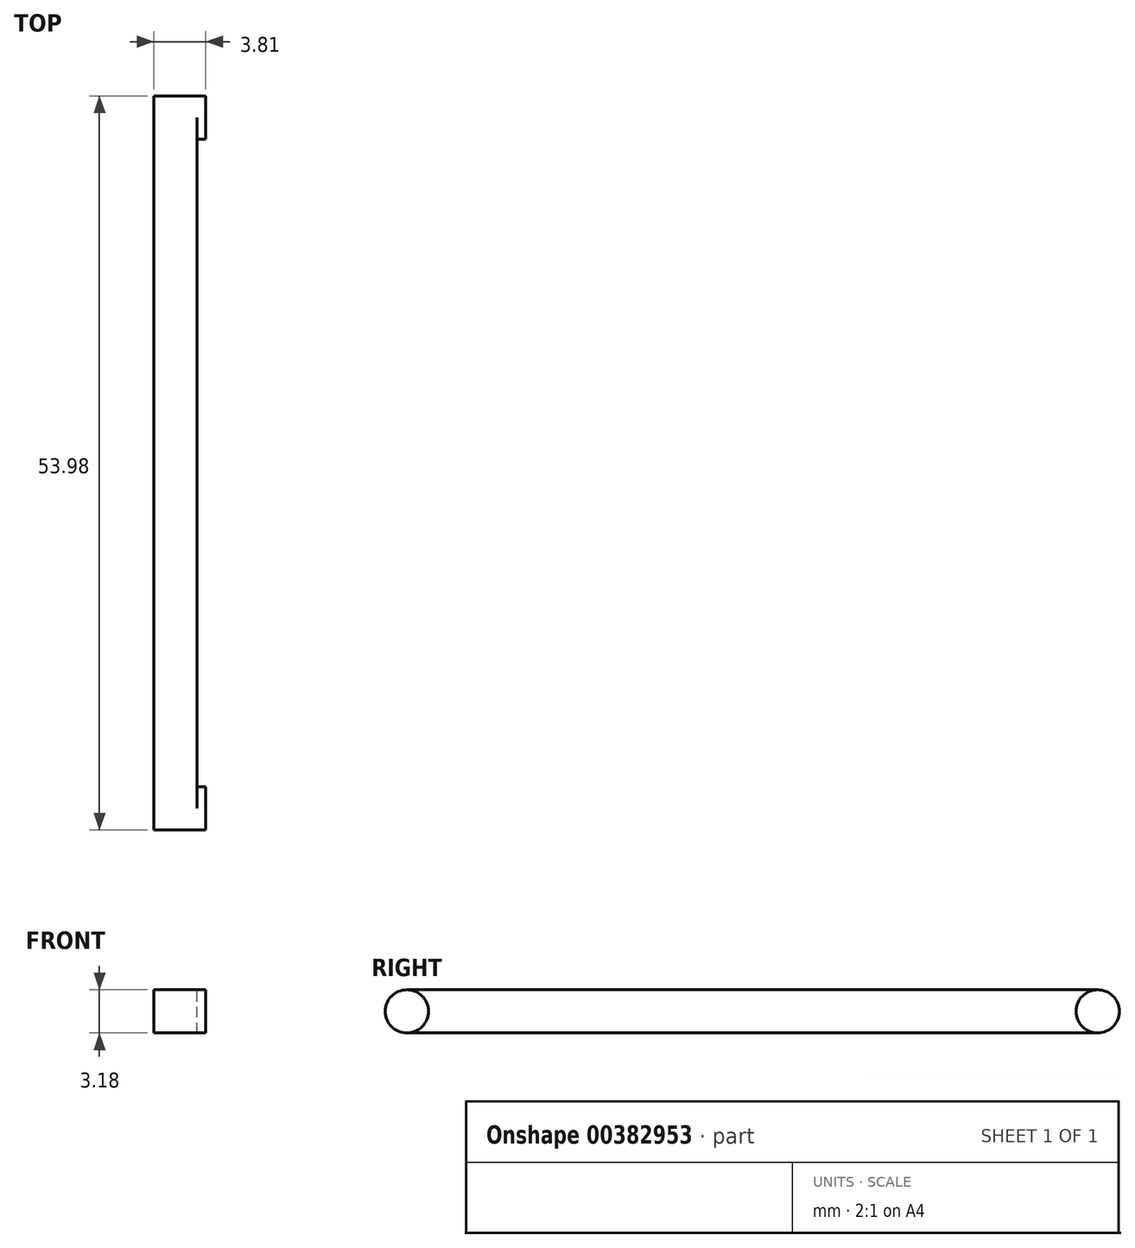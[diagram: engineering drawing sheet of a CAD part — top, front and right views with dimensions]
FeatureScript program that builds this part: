
annotation { "Feature Type Name" : "Feature", "Feature Type Description" : "" }
export const myFeature = defineFeature(function(context is Context, id is Id, definition is map)
    precondition{}
    {
        {
            var Q0;
            Q0=qCreatedBy(makeId("Right.planeOp"),FACE);
            var sketch = newSketch(context, id + "F0", { "sketchPlane" : qUnion([Q0])});
            skLineSegment(sketch, "E0.bottom", {"start": v(25.4, 1.59) * mm, "end": v(-25.4, 1.59) * mm});
            skLineSegment(sketch, "E0.top", {"start": v(25.4, -1.59) * mm, "end": v(-25.4, -1.59) * mm});
            skLineSegment(sketch, "E0.left", {"start": v(25.4, 1.59) * mm, "end": v(25.4, -1.59) * mm});
            skLineSegment(sketch, "E0.right", {"start": v(-25.4, 1.59) * mm, "end": v(-25.4, -1.59) * mm});
            skPoint(sketch, "E0.middle", {"position": v(0, 0) * mm});
            skCircle(sketch, "E1", {"center": v(-25.4, 0) * mm, "radius": 1.59 * mm});
            skCircle(sketch, "E2", {"center": v(25.4, 0) * mm, "radius": 1.59 * mm});
            skSolve(sketch);
        }
        {
            var Q0;
            {var subQ0=sQuery(id+"F0.wireOp",EDGE,"E0.bottom");Q0=makeQuery(id+"F0.imprint","IMPRINT",FACE,{"disambiguationData":[TD([[makeQuery(id+"F0.imprint","IMPRINT",EDGE,{"derivedFrom":subQ0}),1.0]])]});}
            extrude(context, id + "F1", {"entities" : qUnion([Q0]), "depth" : 3.17 * mm});
        }
        {
            var Q0;
            {var subQ0=sQuery(id+"F0.wireOp",EDGE,"E0.right");Q0=makeQuery(id+"F0.imprint","IMPRINT",FACE,{"disambiguationData":[TD([[makeQuery(id+"F0.imprint","IMPRINT",EDGE,{"derivedFrom":subQ0}),1.0]])]});}
            var Q1;
            {var subQ0=sQuery(id+"F0.wireOp",EDGE,"E0.right");Q1=makeQuery(id+"F0.imprint","IMPRINT",FACE,{"disambiguationData":[TD([[makeQuery(id+"F0.imprint","IMPRINT",EDGE,{"derivedFrom":subQ0}),-1.0]])]});}
            var Q2;
            {var subQ0=sQuery(id+"F0.wireOp",EDGE,"E0.left");Q2=makeQuery(id+"F0.imprint","IMPRINT",FACE,{"disambiguationData":[TD([[makeQuery(id+"F0.imprint","IMPRINT",EDGE,{"derivedFrom":subQ0}),1.0]])]});}
            var Q3;
            {var subQ0=sQuery(id+"F0.wireOp",EDGE,"E0.left");Q3=makeQuery(id+"F0.imprint","IMPRINT",FACE,{"disambiguationData":[TD([[makeQuery(id+"F0.imprint","IMPRINT",EDGE,{"derivedFrom":subQ0}),-1.0]])]});}
            extrude(context, id + "F2", {"entities" : qUnion([Q0, Q1, Q2, Q3]), "operationType" : NewBodyOperationType.ADD, "depth" : 3.8 * mm});
        }
    });
